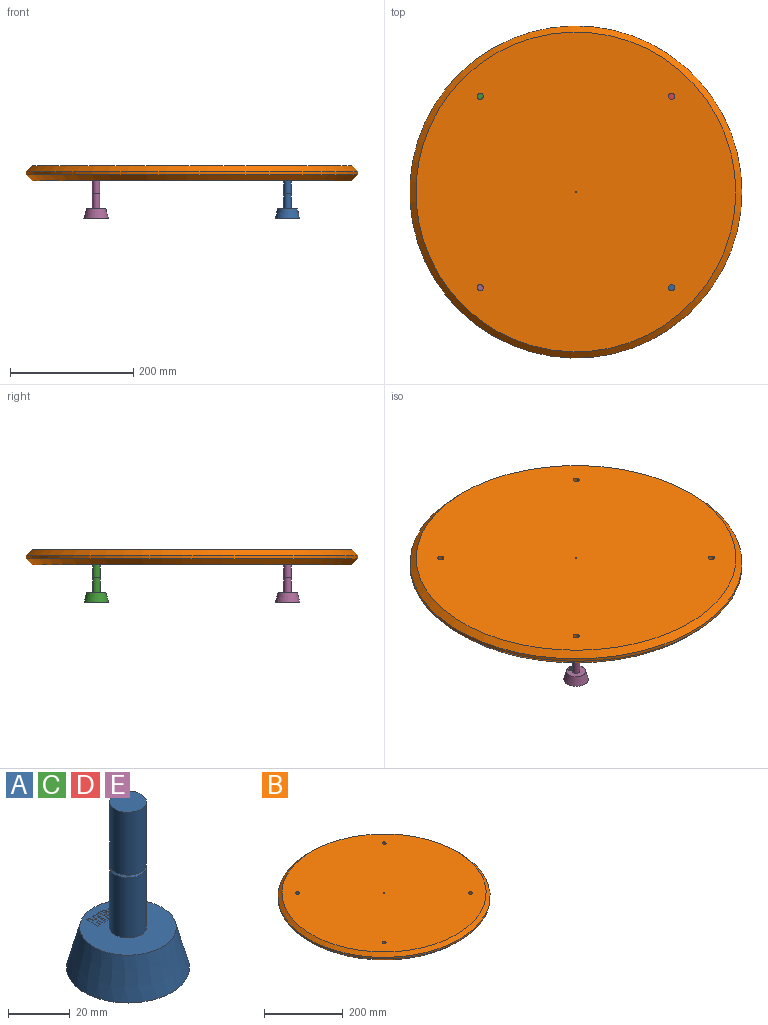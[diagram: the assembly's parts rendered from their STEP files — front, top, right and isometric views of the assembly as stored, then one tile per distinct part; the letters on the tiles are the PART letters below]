
ASSEMBLY  parts=5 mates=1
PART A: 41 faces, bbox 40x40x66 mm
  f0: cone r=4.93mm half-angle=45deg, axis (0,0,-1), area 52.1mm2, adj f1,f40
  f1: cylinder r=6mm len=23.93mm, axis (0,0,1), area 902mm2, adj f0,f2
  f2: plane 31.43x31.43mm, normal (0,0,1), area 624.4mm2, adj f1,f3,f8,f9,f10,f11,f12,f13
  f3: cone r=15.71mm half-angle=15deg, axis (0,0,-1), area 1858.4mm2, adj f2,f4
  f4: plane 40x40mm, normal (0,0,-1), area 942.5mm2, adj f3,f5
  f5: cylinder r=10mm len=20mm, axis (0,0,1), area 117.3mm2, adj f4,f6
  f6: torus R=9.2mm, axis (0,0,-1), area 76.7mm2, adj f5,f7
  f7: plane 18.4x18.4mm, normal (0,0,-1), area 265.9mm2, adj f6
  f8: plane 1.25x0.1mm, normal (0,-1,0), area 0.1mm2, adj f2,f9,f19,f20
  f9: plane 5x0.1mm, normal (1,0,0), area 0.5mm2, adj f2,f8,f10,f20
  f10: plane 1.25x0.1mm, normal (0,1,0), area 0.1mm2, adj f2,f9,f11,f20
  f11: plane 1.88x0.1mm, normal (-1,0,0), area 0.2mm2, adj f2,f10,f12,f20
  f12: plane 1.25x0.1mm, normal (0,1,0), area 0.1mm2, adj f2,f11,f13,f20
  f13: plane 1.88x0.1mm, normal (1,0,0), area 0.2mm2, adj f2,f12,f14,f20
  f14: plane 1.25x0.1mm, normal (0,1,0), area 0.1mm2, adj f2,f13,f15,f20
  f15: plane 5x0.1mm, normal (-1,0,0), area 0.5mm2, adj f2,f14,f16,f20
  f16: plane 1.25x0.1mm, normal (0,-1,0), area 0.1mm2, adj f2,f15,f17,f20
  f17: plane 1.88x0.1mm, normal (1,0,0), area 0.2mm2, adj f2,f16,f18,f20
  f18: plane 1.25x0.1mm, normal (0,-1,0), area 0.1mm2, adj f2,f17,f19,f20
  f19: plane 1.88x0.1mm, normal (-1,0,0), area 0.2mm2, adj f2,f8,f18,f20
  f20: plane 5x3.75mm, normal (0,0,1), area 14.1mm2, adj f8,f9,f10,f11,f12,f13,f14,f15
  f21: plane 2.2x0.1mm, normal (0,-1,0), area 0.2mm2, adj f2,f22,f30,f31
  f22: plane 5x0.1mm, normal (1,0,0), area 0.5mm2, adj f2,f21,f23,f31
  f23: plane 1.25x0.1mm, normal (0,1,0), area 0.1mm2, adj f2,f22,f24,f31
  f24: plane 1.88x0.1mm, normal (-1,0,0), area 0.2mm2, adj f2,f23,f25,f31
  f25: plane 0.95x0.1mm, normal (0,1,0), area 0.1mm2, adj f2,f24,f30,f31
  f26: plane 0.95x0.1mm, normal (0,1,0), area 0.1mm2, adj f27,f29,f31,f32
  f27: cylinder r=0.62mm len=1.25mm, axis (0,0,-1), area 0.2mm2, adj f26,f28,f31,f32
  f28: plane 0.95x0.1mm, normal (0,-1,0), area 0.1mm2, adj f27,f29,f31,f32
  f29: plane 1.25x0.1mm, normal (-1,0,0), area 0.1mm2, adj f26,f28,f31,f32
  f30: cylinder r=1.56mm len=3.13mm, axis (0,0,-1), area 0.5mm2, adj f2,f21,f25,f31
  f31: plane 5x3.76mm, normal (0,0,1), area 11.3mm2, adj f21,f22,f23,f24,f25,f26,f27,f28
  f32: plane 1.58x1.25mm, normal (0,0,1), area 1.8mm2, adj f26,f27,f28,f29
  f33: plane 0.88x0.88mm, normal (-0.71,0.71,0), area 0.1mm2, adj f2,f34,f36,f37
  f34: cylinder r=2.5mm len=5mm, axis (0,0,-1), area 1.2mm2, adj f2,f33,f35,f37
  f35: plane 0.88x0.88mm, normal (-0.71,-0.71,0), area 0.1mm2, adj f2,f34,f36,f37
  f36: cylinder r=1.25mm len=2.5mm, axis (0,0,-1), area 0.6mm2, adj f2,f33,f35,f37
  f37: plane 5x4.27mm, normal (0,0,1), area 11mm2, adj f33,f34,f35,f36
  f38: cylinder r=6mm len=25mm, axis (0,0,-1), area 942.5mm2, adj f39,f40
  f39: plane 12x12mm, normal (0,0,1), area 113.1mm2, adj f38
  f40: plane 12x12mm, normal (0,0,-1), area 36.8mm2, adj f0,f38
PART B: 10 faces, bbox 540x540x25 mm
  f0: cylinder r=270mm len=540mm, axis (0,0,-1), area 8482.3mm2, adj f3,f4
  f1: plane 520x520mm, normal (0,0,1), area 212056.7mm2, adj f3,f5,f6,f7,f8,f9
  f2: plane 520x520mm, normal (0,0,-1), area 212056.7mm2, adj f4,f5,f6,f7,f8,f9
  f3: cone r=260mm half-angle=45deg, axis (0,0,-1), area 23547.3mm2, adj f0,f1
  f4: cone r=270mm half-angle=45deg, axis (0,0,1), area 23547.3mm2, adj f0,f2
  f5: cylinder r=0.5mm len=25mm, axis (0,0,1), area 78.5mm2, adj f1,f2
  f6: cylinder r=5mm len=25mm, axis (0,0,1), area 785.4mm2, adj f1,f2
  f7: cylinder r=5mm len=25mm, axis (0,0,1), area 785.4mm2, adj f1,f2
  f8: cylinder r=5mm len=25mm, axis (0,0,1), area 785.4mm2, adj f1,f2
  f9: cylinder r=5mm len=25mm, axis (0,0,1), area 785.4mm2, adj f1,f2
PART C: same geometry as A
PART D: same geometry as A
PART E: same geometry as A
PLACE A rot(axis=(0,0,1),90deg) t=(155.56,-155.56,-86)mm
PLACE B t=(0,0,-25)mm
PLACE C rot(axis=(0,0,-1),90deg) t=(-155.56,155.56,-86)mm
PLACE D rot(axis=(0,0,1),180deg) t=(155.56,155.56,-86)mm
PLACE E t=(-155.56,-155.56,-86)mm
MATE fastened E.f1 <-> B.f9  axis (0,0,1) through (-155.56,-155.56,-70)mm
